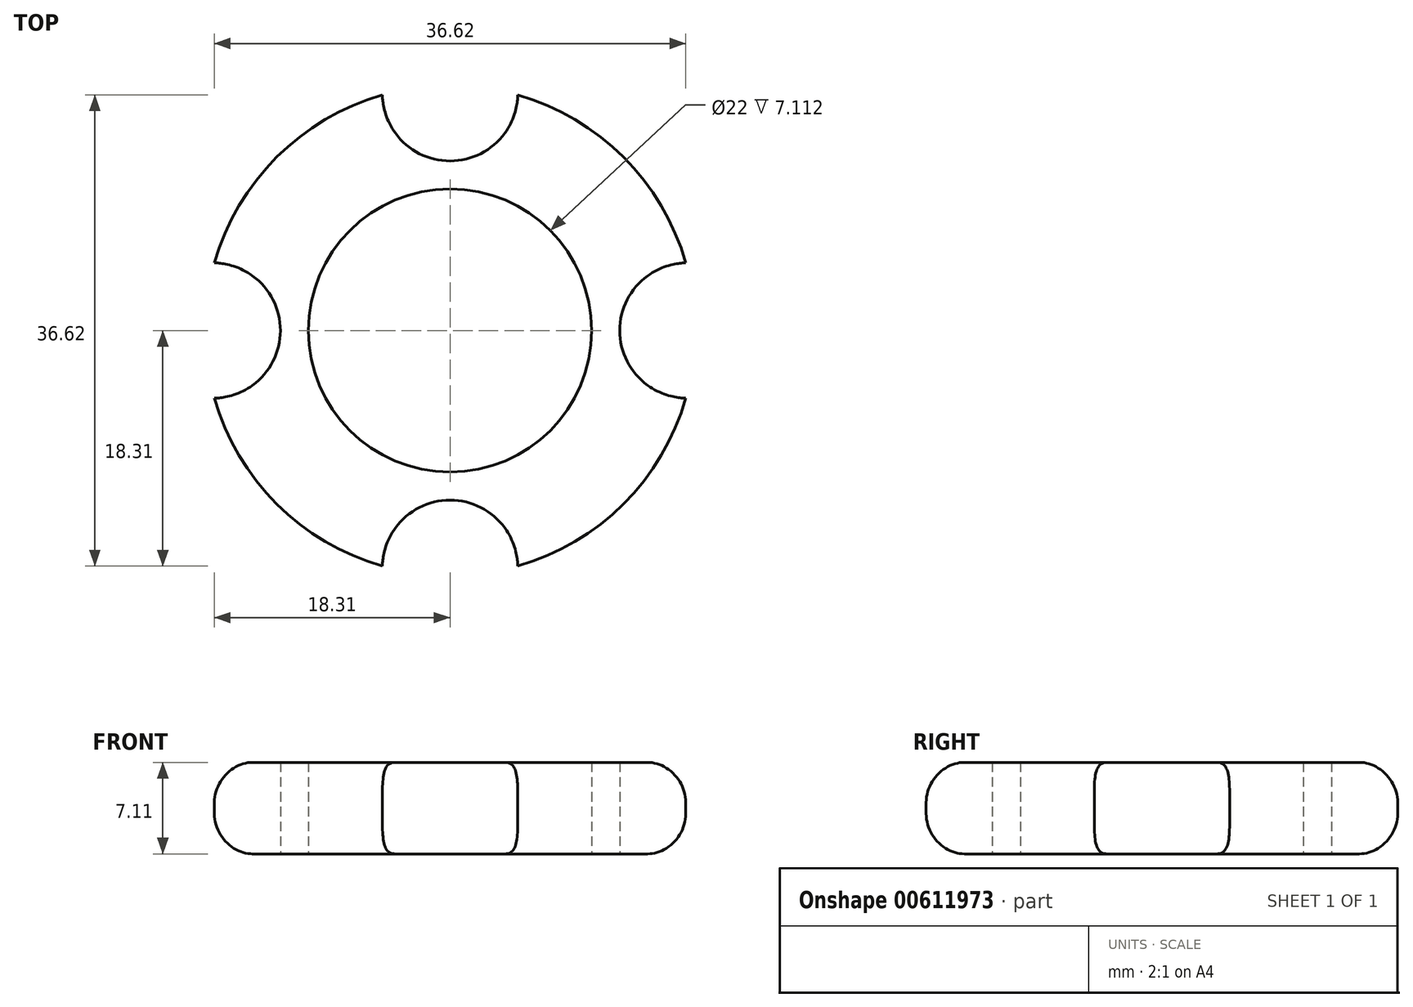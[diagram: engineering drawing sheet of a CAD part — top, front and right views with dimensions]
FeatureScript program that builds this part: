
annotation { "Feature Type Name" : "Feature", "Feature Type Description" : "" }
export const myFeature = defineFeature(function(context is Context, id is Id, definition is map)
    precondition{}
    {
        {
            var Q0;
            Q0=qCreatedBy(makeId("Top.planeOp"),FACE);
            var sketch = newSketch(context, id + "F0", { "sketchPlane" : qUnion([Q0])});
            skArc(sketch, "E0", {"start": v(-5.26, 18.31) * mm, "mid": v(-13.47, 13.47) * mm, "end": v(-18.31, 5.26) * mm});
            skCircle(sketch, "E1", {"center": v(0, 0) * mm, "radius": 11 * mm});
            skArc(sketch, "E2", {"start": v(-5.26, 18.31) * mm, "mid": v(0, 13.18) * mm, "end": v(5.26, 18.31) * mm});
            skArc(sketch, "E3", {"start": v(18.31, 5.26) * mm, "mid": v(13.18, 0) * mm, "end": v(18.31, -5.26) * mm});
            skArc(sketch, "E4", {"start": v(-18.31, -5.26) * mm, "mid": v(-13.18, 0) * mm, "end": v(-18.31, 5.26) * mm});
            skArc(sketch, "E5", {"start": v(5.26, -18.31) * mm, "mid": v(0, -13.18) * mm, "end": v(-5.26, -18.31) * mm});
            skPoint(sketch, "E6.start.orphan", {"position": v(11, 0) * mm});
            skPoint(sketch, "E7.start.orphan", {"position": v(0, -11) * mm});
            skPoint(sketch, "E8.start.orphan", {"position": v(-11, 0) * mm});
            skArc(sketch, "E9.trimOffspring", {"start": v(-18.31, -5.26) * mm, "mid": v(-13.47, -13.47) * mm, "end": v(-5.26, -18.31) * mm});
            skArc(sketch, "E10.trimOffspring", {"start": v(18.31, 5.26) * mm, "mid": v(13.47, 13.47) * mm, "end": v(5.26, 18.31) * mm});
            skArc(sketch, "E11.trimOffspring", {"start": v(5.26, -18.31) * mm, "mid": v(13.47, -13.47) * mm, "end": v(18.31, -5.26) * mm});
            skSolve(sketch);
        }
        {
            var Q0;
            Q0 = qSketchRegion(id + "F0", true);
            extrude(context, id + "F1", {"entities" : qUnion([Q0]), "depth" : 7.11 * mm, "offsetDistance" : 25.4 * mm});
        }
        {
            var Q0;
            Q0=makeQuery(id+"F1.opExtrude","CAP_EDGE",EDGE,{"disambiguationData":[OSD([sQuery(id+"F0.wireOp",EDGE,"E0")])],"isStart":false});
            var Q1;
            Q1=makeQuery(id+"F1.opExtrude","CAP_EDGE",EDGE,{"disambiguationData":[OSD([sQuery(id+"F0.wireOp",EDGE,"E9.trimOffspring")])],"isStart":false});
            var Q2;
            Q2=makeQuery(id+"F1.opExtrude","CAP_EDGE",EDGE,{"disambiguationData":[OSD([sQuery(id+"F0.wireOp",EDGE,"E11.trimOffspring")])],"isStart":false});
            var Q3;
            Q3=makeQuery(id+"F1.opExtrude","CAP_EDGE",EDGE,{"disambiguationData":[OSD([sQuery(id+"F0.wireOp",EDGE,"E10.trimOffspring")])],"isStart":false});
            var Q4;
            Q4=makeQuery(id+"F1.opExtrude","CAP_EDGE",EDGE,{"disambiguationData":[OSD([sQuery(id+"F0.wireOp",EDGE,"E10.trimOffspring")])],"isStart":true});
            var Q5;
            Q5=makeQuery(id+"F1.opExtrude","CAP_EDGE",EDGE,{"disambiguationData":[OSD([sQuery(id+"F0.wireOp",EDGE,"E0")])],"isStart":true});
            var Q6;
            Q6=makeQuery(id+"F1.opExtrude","CAP_EDGE",EDGE,{"disambiguationData":[OSD([sQuery(id+"F0.wireOp",EDGE,"E9.trimOffspring")])],"isStart":true});
            var Q7;
            Q7=makeQuery(id+"F1.opExtrude","CAP_EDGE",EDGE,{"disambiguationData":[OSD([sQuery(id+"F0.wireOp",EDGE,"E11.trimOffspring")])],"isStart":true});
            fillet(context, id + "F2", {"entities" : qUnion([Q0, Q1, Q2, Q3, Q4, Q5, Q6, Q7]), "radius" : 3.12 * mm, "tangentPropagation" : true, "allowEdgeOverflow" : false});
        }
    });
